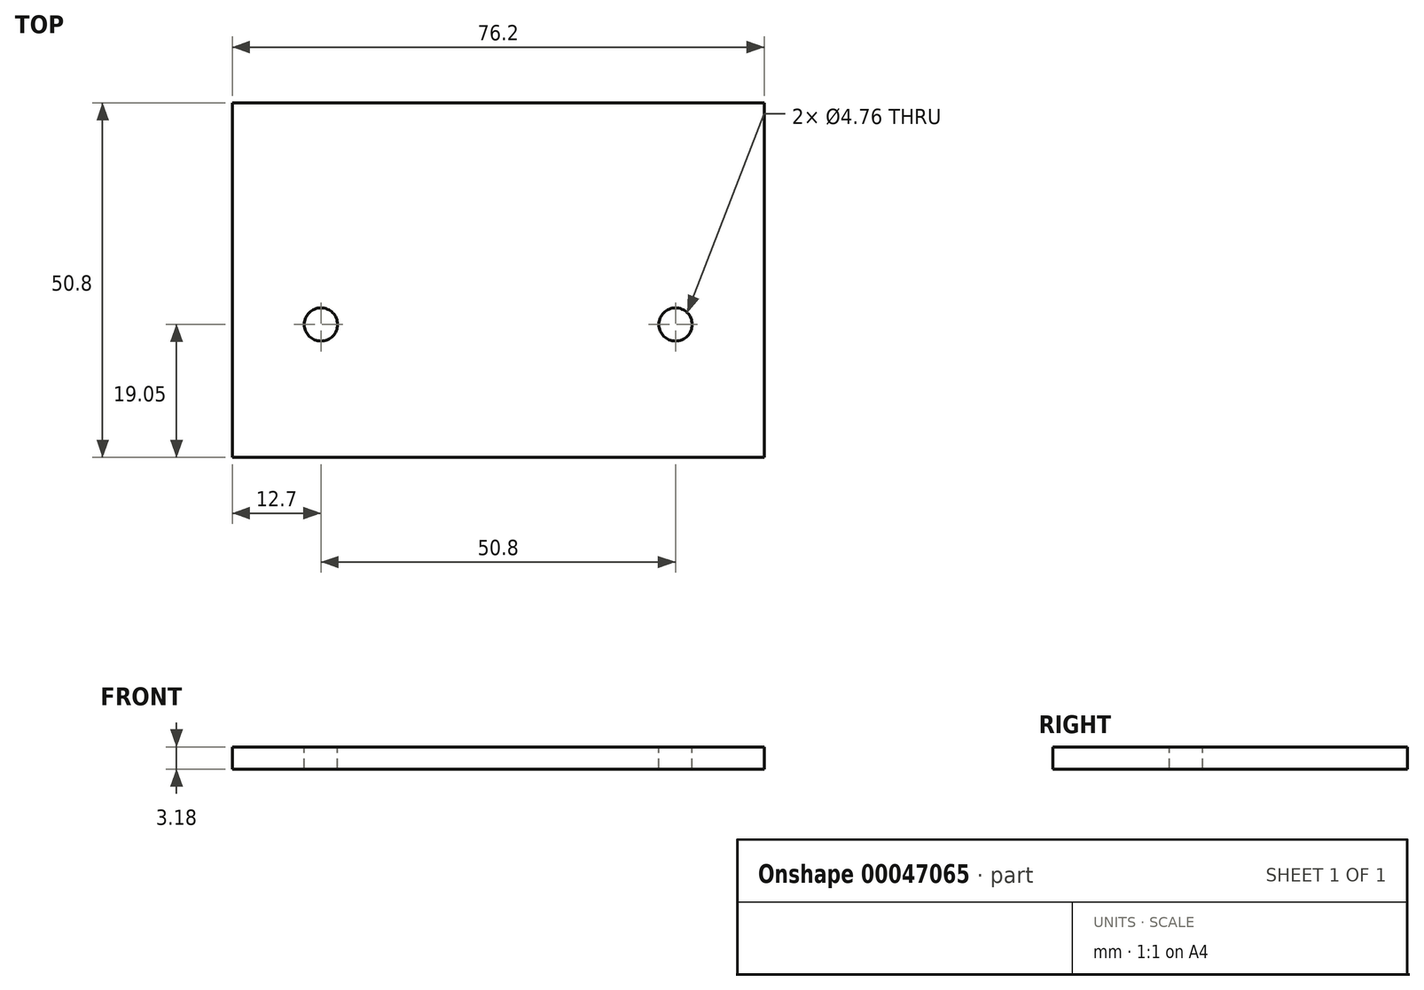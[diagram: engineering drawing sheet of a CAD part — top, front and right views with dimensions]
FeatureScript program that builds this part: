
annotation { "Feature Type Name" : "Feature", "Feature Type Description" : "" }
export const myFeature = defineFeature(function(context is Context, id is Id, definition is map)
    precondition{}
    {
        {
            var Q0;
            Q0=qCreatedBy(makeId("Top.planeOp"),FACE);
            var sketch = newSketch(context, id + "F0", { "sketchPlane" : qUnion([Q0])});
            skLineSegment(sketch, "E0.rect.bottom", {"start": v(38.1, 25.4) * mm, "end": v(-38.1, 25.4) * mm});
            skLineSegment(sketch, "E0.rect.top", {"start": v(38.1, -25.4) * mm, "end": v(-38.1, -25.4) * mm});
            skLineSegment(sketch, "E0.rect.left", {"start": v(38.1, 25.4) * mm, "end": v(38.1, -25.4) * mm});
            skLineSegment(sketch, "E0.rect.right", {"start": v(-38.1, 25.4) * mm, "end": v(-38.1, -25.4) * mm});
            skPoint(sketch, "E0.rect.middle", {"position": v(0, 0) * mm});
            skSolve(sketch);
        }
        {
            var Q0;
            Q0=makeQuery(id+"F0.imprint","IMPRINT",FACE,{"disambiguationData":[TD([[makeQuery(id+"F0.imprint","IMPRINT",EDGE,{"derivedFrom":sQuery(id+"F0.wireOp",EDGE,"E0.rect.bottom")}),1.0]])]});
            extrude(context, id + "F1", {"entities" : qUnion([Q0]), "endBound" : BoundingType.SYMMETRIC, "depth" : 3.17 * mm});
        }
        {
            var Q0;
            Q0=makeQuery(id+"F1.opExtrude","CAP_FACE",FACE,{"disambiguationData":[OSD([sQuery(id+"F0.wireOp",EDGE,"E0.rect.bottom"),sQuery(id+"F0.wireOp",EDGE,"E0.rect.top"),sQuery(id+"F0.wireOp",EDGE,"E0.rect.left"),sQuery(id+"F0.wireOp",EDGE,"E0.rect.right")])],"isStart":false});
            var sketch = newSketch(context, id + "F2", { "sketchPlane" : qUnion([Q0])});
            skCircle(sketch, "E1", {"center": v(-25.4, -6.35) * mm, "radius": 2.38 * mm});
            skCircle(sketch, "E2.MirrorC", {"center": v(25.4, -6.35) * mm, "radius": 2.38 * mm});
            skSolve(sketch);
        }
        {
            var Q0;
            Q0 = qSketchRegion(id + "F2", true);
            extrude(context, id + "F3", {"entities" : qUnion([Q0]), "operationType" : NewBodyOperationType.REMOVE, "endBound" : BoundingType.UP_TO_NEXT, "oppositeDirection" : true, "depth" : 25.4 * mm});
        }
    });
